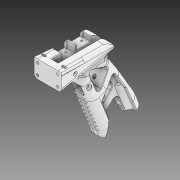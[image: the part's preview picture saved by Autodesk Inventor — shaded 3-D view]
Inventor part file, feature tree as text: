
AUTODESK INVENTOR PART (.ipt)
format: ipt  version: 2020 (Build 240168000, 168)  size: 1,708,032 bytes
history: native  units: in
note: dims shown in document units (in); Inventor stores cm internally (conversion verified against a paired STEP export)
features: extrude x10, sketch x10, fillet x1, plane x1, imported_body x1
ambient origin geometry x8: Origin, YZ Plane, XZ Plane, XY Plane, X Axis, Y Axis, Z Axis, Center Point
bodies: Solid1 (feature_tree)
feature tree (23):
  extrude  "Extrusion1"  Depth=0.1575in
  extrude  "Extrusion4"  Depth=0.3937in TaperAngle=0.0deg
  fillet  "Fillet1"  Radius=0.1378in
  extrude  "Extrusion5"  Depth=0.5906in
  extrude  "Extrusion6"  Depth=0.4724in TaperAngle=0.0deg
  plane  "Work Plane1"
  extrude  "Extrusion7"  Depth=0.2244in
  extrude  "Extrusion8"  Depth=0.4331in
  extrude  "Extrusion9"  Depth=0.9449in
  extrude  "Extrusion10"  Depth=0.3937in
  extrude  "Extrusion11"  Depth=0.0787in TaperAngle=0.0deg
  extrude  "Test Cut"  Depth=0.0394in
  sketch  "Sketch1"  dims[d0=0.0in d1=0.0in d2=0.1575in]
  sketch  "Sketch5"  dims[d7=3.3563in d8=0.0in d9=0.3937in d10=0.0in d11=0.1378in]
  sketch  "Sketch6"  dims[d12=1.1024in d13=0.5906in]
  sketch  "Sketch7"  dims[d14=0.4724in d15=0.5906in d16=0.0in]
  sketch  "Sketch8"  dims[d17=-0.3937in d18=0.2244in]
  sketch  "Sketch10"  dims[d19=0.1024in d20=0.0in d21=0.4331in]
  sketch  "Sketch11"  dims[d22=0.7874in d23=0.9449in]
  sketch  "Sketch12"  dims[d24=0.3937in d25=0.0in d26=0.7874in]
  sketch  "Sketch13"  dims[d27=0.0787in d28=0.2756in d29=0.0in]
  sketch  "Sketch14"  dims[d30=0.0394in d31=0.0394in d32=0.0394in d33=0.0394in d34=0.3642in d35=0.1181in d36=0.0984in d37=0.1969in d38=0.0in d39=0.3642in d40=0.1181in d41=0.0984in d42=0.1772in d43=0.0in d44=0.0in d45=0.0in]
  imported_body  "Base1"
